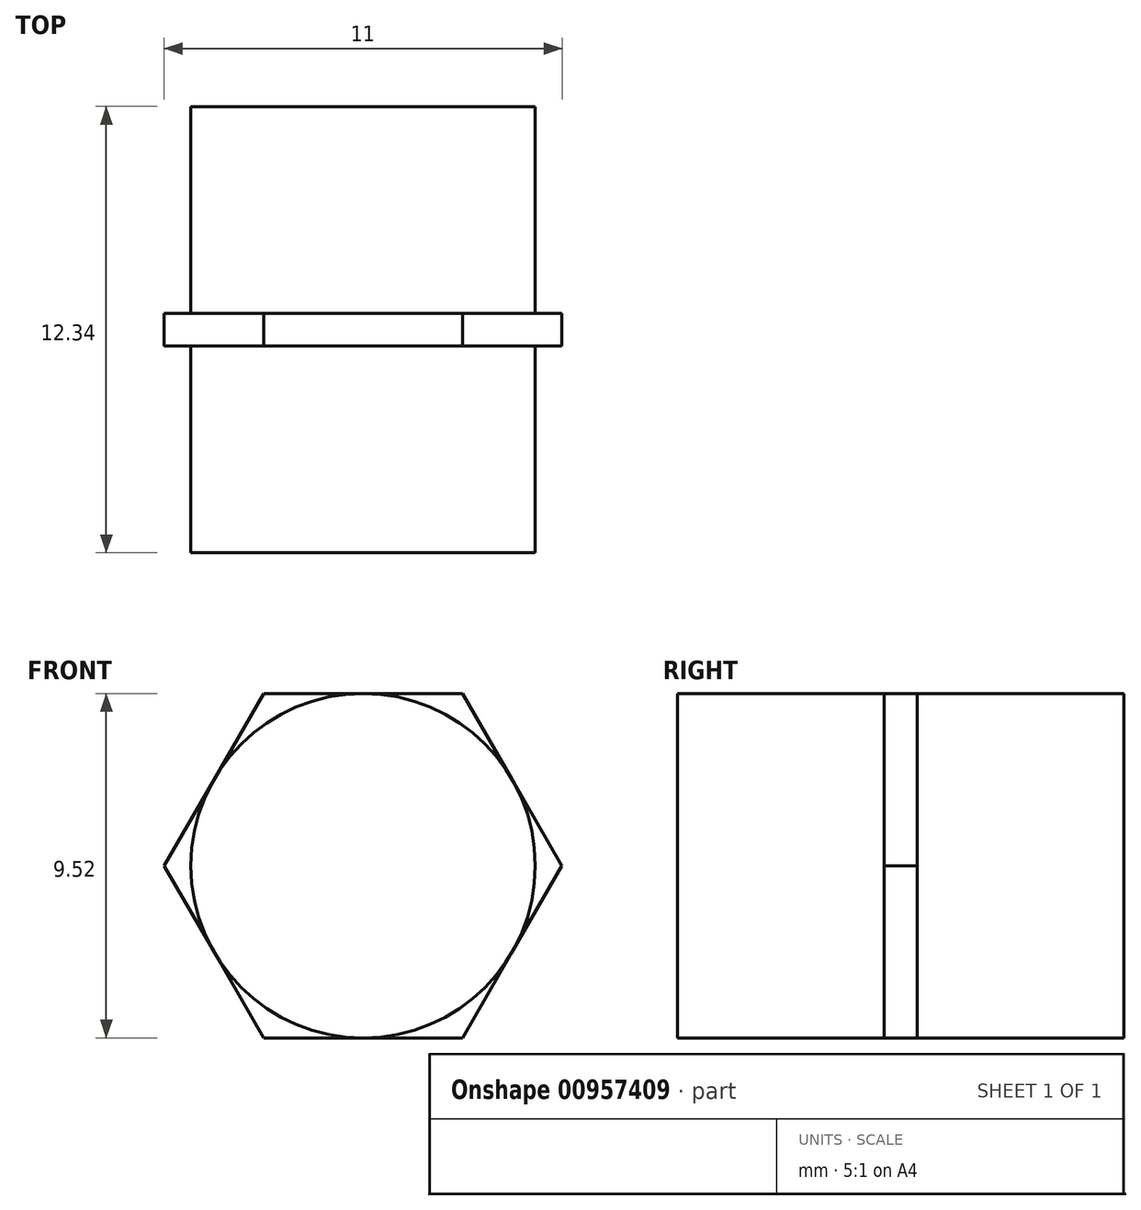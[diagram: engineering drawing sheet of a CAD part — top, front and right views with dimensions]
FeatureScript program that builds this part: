
annotation { "Feature Type Name" : "Feature", "Feature Type Description" : "" }
export const myFeature = defineFeature(function(context is Context, id is Id, definition is map)
    precondition{}
    {
        {
            var Q0;
            Q0=qCreatedBy(makeId("Front.planeOp"),FACE);
            var sketch = newSketch(context, id + "F0", { "sketchPlane" : qUnion([Q0])});
            skCircle(sketch, "E0.cCircle", {"center": v(0, 0) * mm, "radius": 4.76 * mm, "construction": true});
            skLineSegment(sketch, "E0.0", {"start": v(-2.75, 4.76) * mm, "end": v(2.75, 4.76) * mm});
            skLineSegment(sketch, "E0.1", {"start": v(2.75, 4.76) * mm, "end": v(5.5, 0) * mm});
            skLineSegment(sketch, "E0.2", {"start": v(5.5, 0) * mm, "end": v(2.75, -4.76) * mm});
            skLineSegment(sketch, "E0.3", {"start": v(2.75, -4.76) * mm, "end": v(-2.75, -4.76) * mm});
            skLineSegment(sketch, "E0.4", {"start": v(-2.75, -4.76) * mm, "end": v(-5.5, 0) * mm});
            skLineSegment(sketch, "E0.5", {"start": v(-5.5, 0) * mm, "end": v(-2.75, 4.76) * mm});
            skPoint(sketch, "E0.0.midPoint", {"position": v(0, 4.76) * mm});
            skSolve(sketch);
        }
        {
            var Q0;
            Q0 = qSketchRegion(id + "F0", true);
            extrude(context, id + "F1", {"entities" : qUnion([Q0]), "depth" : (1.03 - (.125)) * mm, "offsetDistance" : 25.4 * mm});
        }
        {
            var Q0;
            Q0=makeQuery(id+"F1.opExtrude","CAP_FACE",FACE,{"disambiguationData":[OSD([sQuery(id+"F0.wireOp",EDGE,"E0.0"),sQuery(id+"F0.wireOp",EDGE,"E0.1"),sQuery(id+"F0.wireOp",EDGE,"E0.2"),sQuery(id+"F0.wireOp",EDGE,"E0.3"),sQuery(id+"F0.wireOp",EDGE,"E0.4"),sQuery(id+"F0.wireOp",EDGE,"E0.5")])],"isStart":false});
            var sketch = newSketch(context, id + "F2", { "sketchPlane" : qUnion([Q0])});
            skCircle(sketch, "E1", {"center": v(0, 0) * mm, "radius": 4.76 * mm});
            skSolve(sketch);
        }
        {
            var Q0;
            Q0 = qSketchRegion(id + "F2", true);
            extrude(context, id + "F3", {"entities" : qUnion([Q0]), "operationType" : NewBodyOperationType.ADD, "depth" : 5.7 * mm, "offsetDistance" : 25.4 * mm});
        }
        {
            var Q0;
            Q0=makeQuery(id+"F1.opExtrude","CAP_FACE",FACE,{"disambiguationData":[OSD([sQuery(id+"F0.wireOp",EDGE,"E0.0"),sQuery(id+"F0.wireOp",EDGE,"E0.1"),sQuery(id+"F0.wireOp",EDGE,"E0.2"),sQuery(id+"F0.wireOp",EDGE,"E0.3"),sQuery(id+"F0.wireOp",EDGE,"E0.4"),sQuery(id+"F0.wireOp",EDGE,"E0.5")])],"isStart":true});
            var sketch = newSketch(context, id + "F4", { "sketchPlane" : qUnion([Q0])});
            skCircle(sketch, "E2", {"center": v(0, 0) * mm, "radius": 4.76 * mm});
            skSolve(sketch);
        }
        {
            var Q0;
            Q0 = qSketchRegion(id + "F4", true);
            extrude(context, id + "F5", {"entities" : qUnion([Q0]), "operationType" : NewBodyOperationType.ADD, "depth" : 5.7 * mm, "offsetDistance" : 25.4 * mm});
        }
    });
